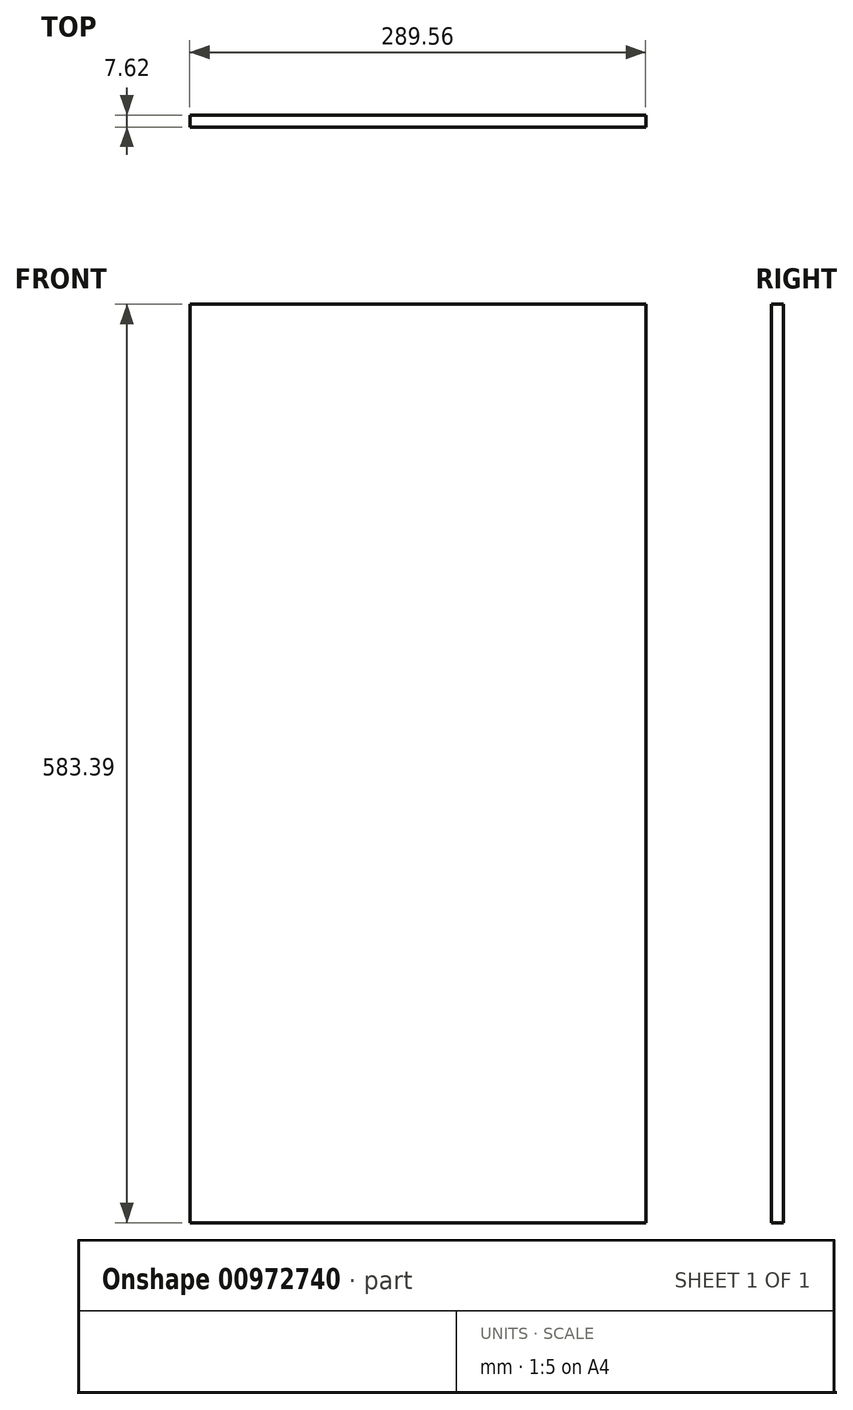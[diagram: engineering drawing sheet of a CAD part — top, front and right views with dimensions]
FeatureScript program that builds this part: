
annotation { "Feature Type Name" : "Feature", "Feature Type Description" : "" }
export const myFeature = defineFeature(function(context is Context, id is Id, definition is map)
    precondition{}
    {
        {
            var Q0;
            Q0=qCreatedBy(makeId("Front.planeOp"),FACE);
            var sketch = newSketch(context, id + "F0", { "sketchPlane" : qUnion([Q0])});
            skLineSegment(sketch, "E0.bottom", {"start": v(5.83, 0) * mm, "end": v(295.4, 0) * mm});
            skLineSegment(sketch, "E0.top", {"start": v(5.83, 583.39) * mm, "end": v(295.4, 583.39) * mm});
            skLineSegment(sketch, "E0.left", {"start": v(5.83, 0) * mm, "end": v(5.83, 583.39) * mm});
            skLineSegment(sketch, "E0.right", {"start": v(295.4, 0) * mm, "end": v(295.4, 583.39) * mm});
            skSolve(sketch);
        }
        {
            var Q0;
            Q0 = qSketchRegion(id + "F0", true);
            extrude(context, id + "F1", {"entities" : qUnion([Q0]), "depth" : 7.62 * mm, "offsetDistance" : 25.4 * mm});
        }
    });
